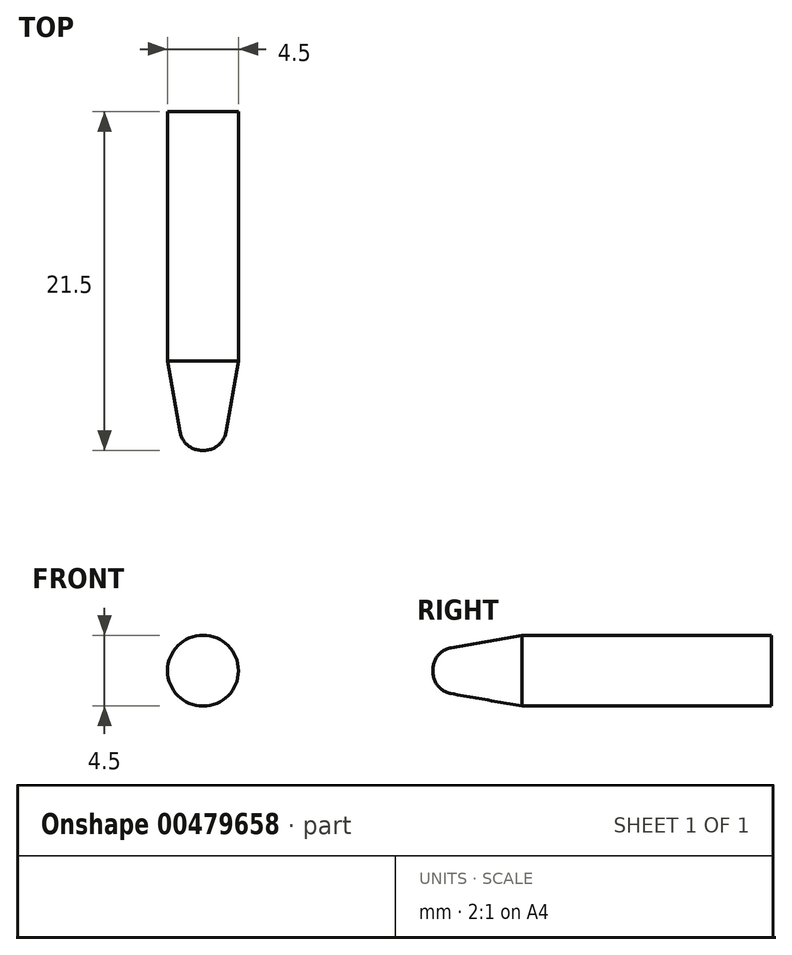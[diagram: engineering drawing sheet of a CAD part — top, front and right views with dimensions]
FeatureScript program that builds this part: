
annotation { "Feature Type Name" : "Feature", "Feature Type Description" : "" }
export const myFeature = defineFeature(function(context is Context, id is Id, definition is map)
    precondition{}
    {
        {
            var Q0;
            Q0=qCreatedBy(makeId("Front.planeOp"),FACE);
            var sketch = newSketch(context, id + "F0", { "sketchPlane" : qUnion([Q0])});
            skCircle(sketch, "E0", {"center": v(0, 0) * mm, "radius": 2.25 * mm});
            skSolve(sketch);
        }
        {
            var Q0;
            Q0=makeQuery(id+"F0.imprint","IMPRINT",FACE,{"disambiguationData":[TD([[makeQuery(id+"F0.imprint","IMPRINT",EDGE,{"derivedFrom":sQuery(id+"F0.wireOp",EDGE,"E0")}),1.0]])]});
            var Q1;
            Q1=sQuery(id+"F0.wireOp",EDGE,"E0");
            extrude(context, id + "F1", {"entities" : qUnion([Q0]), "surfaceEntities" : qUnion([Q1]), "depth" : 21.5 * mm});
        }
        {
            var Q0;
            Q0=makeQuery(id+"F1.opExtrude","CAP_FACE",FACE,{"disambiguationData":[OSD([sQuery(id+"F0.wireOp",EDGE,"E0")])],"isStart":false});
            chamfer(context, id + "F2", {"entities" : qUnion([Q0]), "chamferType" : ChamferType.OFFSET_ANGLE, "width" : 1 * mm, "oppositeDirection" : false, "angle" : 80 * degree, "tangentPropagation" : true});
        }
        {
            var Q0;
            Q0=makeQuery(id+"F1.opExtrude","CAP_FACE",FACE,{"disambiguationData":[OSD([sQuery(id+"F0.wireOp",EDGE,"E0")])],"isStart":false});
            fillet(context, id + "F3", {"entities" : qUnion([Q0]), "radius" : 1.4 * mm, "tangentPropagation" : true, "allowEdgeOverflow" : false});
        }
    });
